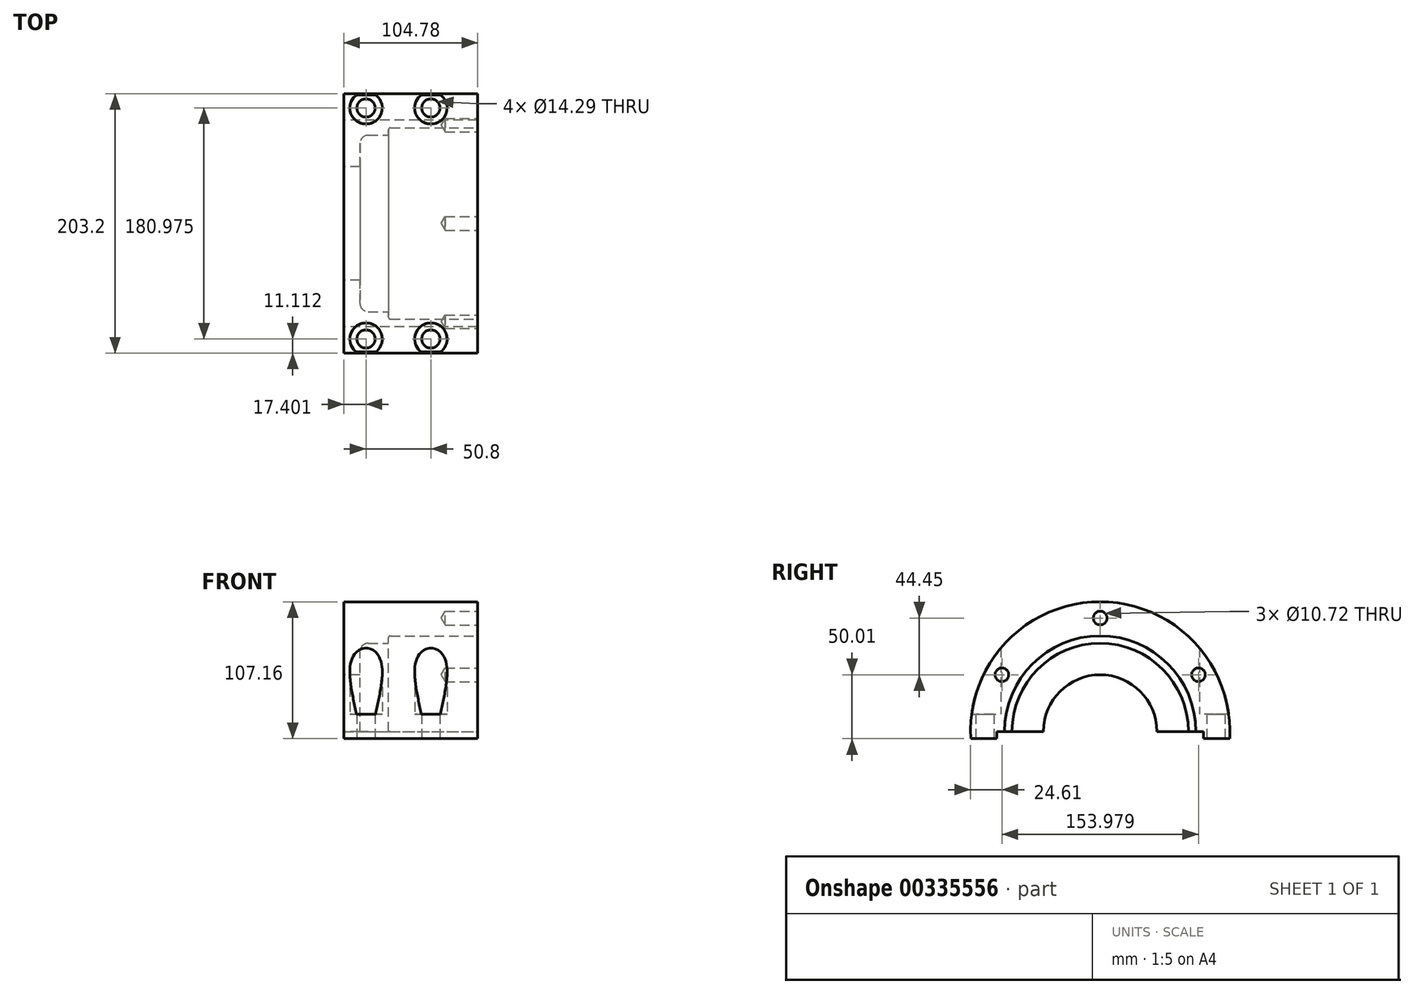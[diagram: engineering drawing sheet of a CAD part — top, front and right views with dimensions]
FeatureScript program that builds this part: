
annotation { "Feature Type Name" : "Feature", "Feature Type Description" : "" }
export const myFeature = defineFeature(function(context is Context, id is Id, definition is map)
    precondition{}
    {
        {
            var Q0;
            Q0=qCreatedBy(makeId("Right.planeOp"),FACE);
            var sketch = newSketch(context, id + "F0", { "sketchPlane" : qUnion([Q0])});
            skCircle(sketch, "E0", {"center": v(0, 0) * mm, "radius": 101.6 * mm});
            skCircle(sketch, "E1", {"center": v(0, 0) * mm, "radius": 44.45 * mm});
            skSolve(sketch);
        }
        {
            var Q0;
            Q0=qSketchRegion(id+"F0",true);
            extrude(context, id + "F1", {"entities" : qUnion([Q0]), "endBound" : BoundingType.SYMMETRIC, "depth" : 104.77 * mm});
        }
        {
            var Q0;
            Q0=makeQuery(id+"F1.opExtrude","CAP_FACE",FACE,{"disambiguationData":[OSD([sQuery(id+"F0.wireOp",EDGE,"E0"),sQuery(id+"F0.wireOp",EDGE,"E1")])],"isStart":false});
            var sketch = newSketch(context, id + "F2", { "sketchPlane" : qUnion([Q0])});
            skCircle(sketch, "E2", {"center": v(0, 0) * mm, "radius": 69.09 * mm});
            skSolve(sketch);
        }
        {
            var Q0;
            Q0=qSketchRegion(id+"F2",true);
            extrude(context, id + "F3", {"entities" : qUnion([Q0]), "operationType" : NewBodyOperationType.REMOVE, "oppositeDirection" : true, "depth" : 92.07 * mm});
        }
        {
            var Q0;
            Q0=makeQuery(id+"F1.opExtrude","CAP_FACE",FACE,{"disambiguationData":[OSD([sQuery(id+"F0.wireOp",EDGE,"E0"),sQuery(id+"F0.wireOp",EDGE,"E1")])],"isStart":false});
            var sketch = newSketch(context, id + "F4", { "sketchPlane" : qUnion([Q0])});
            skCircle(sketch, "E3", {"center": v(0, 0) * mm, "radius": 74.93 * mm});
            skSolve(sketch);
        }
        {
            var Q0;
            Q0=qSketchRegion(id+"F4",true);
            extrude(context, id + "F5", {"entities" : qUnion([Q0]), "operationType" : NewBodyOperationType.REMOVE, "oppositeDirection" : true, "depth" : 69.85 * mm});
        }
        {
            var Q0;
            Q0=makeQuery(id+"F3.boolean.opBoolean","COPY",EDGE,{"derivedFrom":makeQuery(id+"F3.opExtrude","CAP_EDGE",EDGE,{"disambiguationData":[OSD([sQuery(id+"F2.wireOp",EDGE,"E2")])],"isStart":false})});
            fillet(context, id + "F6", {"entities" : qUnion([Q0]), "radius" : 6.35 * mm, "tangentPropagation" : true, "allowEdgeOverflow" : false});
        }
        {
            var Q0;
            Q0=makeQuery(id+"F5.boolean.opBoolean","COPY",EDGE,{"derivedFrom":makeQuery(id+"F5.opExtrude","CAP_EDGE",EDGE,{"disambiguationData":[OSD([sQuery(id+"F4.wireOp",EDGE,"E3")])],"isStart":false})});
            fillet(context, id + "F7", {"entities" : qUnion([Q0]), "radius" : 1.59 * mm, "tangentPropagation" : true, "allowEdgeOverflow" : false});
        }
        {
            var Q0;
            Q0=makeQuery(id+"F1.opExtrude","CAP_FACE",FACE,{"disambiguationData":[OSD([sQuery(id+"F0.wireOp",EDGE,"E0"),sQuery(id+"F0.wireOp",EDGE,"E1")])],"isStart":false});
            var sketch = newSketch(context, id + "F8", { "sketchPlane" : qUnion([Q0])});
            skCircle(sketch, "E4", {"center": v(0, 0) * mm, "radius": 88.9 * mm, "construction": true});
            skLineSegment(sketch, "E5", {"start": v(0, 0) * mm, "end": v(0, 117.43) * mm, "construction": true});
            skLineSegment(sketch, "E6", {"start": v(0, 0) * mm, "end": v(-111.63, 64.45) * mm, "construction": true});
            skPoint(sketch, "E7", {"position": v(-76.99, 44.45) * mm});
            skPoint(sketch, "E8", {"position": v(0, 88.9) * mm});
            skPoint(sketch, "E9.MirrorP", {"position": v(76.99, 44.45) * mm});
            skSolve(sketch);
        }
        {
            var Q0;
            Q0=sQuery(id+"F8.wireOp",VERTEX,"E7");
            var Q1;
            Q1=sQuery(id+"F8.wireOp",VERTEX,"E8");
            var Q2;
            Q2=sQuery(id+"F8.wireOp",VERTEX,"E9.MirrorP");
            var Q3;
            Q3=makeQuery(id+"F1.opExtrude","SWEPT_BODY",BODY,{"disambiguationData":[OSD([sQuery(id+"F0.wireOp",EDGE,"E0"),sQuery(id+"F0.wireOp",EDGE,"E1")])]});
            hole(context, id + "F9", {"style" : HoleStyle.SIMPLE, "endStyle" : HoleEndStyle.BLIND, "standardTappedOrClearance" : lookupTablePath({ "standard" : "ANSI", "engagement" : "75%", "pitch" : "13 tpi", "size" : "1/2", "type" : "Tapped" }), "standardBlindInLast" : lookupTablePath({ "standard" : "ANSI", "engagement" : "75%", "pitch" : "13 tpi", "size" : "1/2", "type" : "Tapped" }), "holeDiameter" : 10.72 * mm, "showTappedDepth" : true, "holeDepth" : 25.4 * mm, "tappedDepth" : 19.53 * mm, "tapClearance" : 3, "locations" : qUnion([Q0, Q1, Q2]), "scope" : qUnion([Q3]), "majorDiameter" : 12.7 * mm});
        }
        {
            var Q0;
            Q0=makeQuery(id+"F1.opExtrude","CAP_FACE",FACE,{"disambiguationData":[OSD([sQuery(id+"F0.wireOp",EDGE,"E0"),sQuery(id+"F0.wireOp",EDGE,"E1")])],"isStart":false});
            var sketch = newSketch(context, id + "F10", { "sketchPlane" : qUnion([Q0])});
            skLineSegment(sketch, "E10", {"start": v(-153.72, 0) * mm, "end": v(137.98, 0) * mm, "construction": true});
            skLineSegment(sketch, "E11.0", {"start": v(-153.72, -5.56) * mm, "end": v(137.98, -5.56) * mm, "construction": true});
            skLineSegment(sketch, "E12.bottom", {"start": v(-150.99, -5.56) * mm, "end": v(143.45, -5.56) * mm});
            skLineSegment(sketch, "E12.top", {"start": v(-150.99, -114.35) * mm, "end": v(143.45, -114.35) * mm});
            skLineSegment(sketch, "E12.left", {"start": v(-150.99, -5.56) * mm, "end": v(-150.99, -114.35) * mm});
            skLineSegment(sketch, "E12.right", {"start": v(143.45, -5.56) * mm, "end": v(143.45, -114.35) * mm});
            skSolve(sketch);
        }
        {
            var Q0;
            Q0=qSketchRegion(id+"F10",true);
            extrude(context, id + "F11", {"entities" : qUnion([Q0]), "operationType" : NewBodyOperationType.REMOVE, "endBound" : BoundingType.THROUGH_ALL, "oppositeDirection" : true, "depth" : 25.4 * mm});
        }
        {
            var Q0;
            Q0=makeQuery(id+"F1.opExtrude","CAP_FACE",FACE,{"disambiguationData":[OSD([sQuery(id+"F0.wireOp",EDGE,"E0"),sQuery(id+"F0.wireOp",EDGE,"E1")])],"isStart":false});
            var sketch = newSketch(context, id + "F12", { "sketchPlane" : qUnion([Q0])});
            skLineSegment(sketch, "E13", {"start": v(-147.56, 0) * mm, "end": v(159.2, 0) * mm, "construction": true});
            skLineSegment(sketch, "E14", {"start": v(0, 129.5) * mm, "end": v(0, -54.35) * mm, "construction": true});
            skLineSegment(sketch, "E15.0", {"start": v(-80.96, 129.5) * mm, "end": v(-80.96, -54.35) * mm, "construction": true});
            skLineSegment(sketch, "E16.bottom", {"start": v(-80.96, 0) * mm, "end": v(80.96, 0) * mm});
            skLineSegment(sketch, "E16.top", {"start": v(-80.96, -25.4) * mm, "end": v(80.96, -25.4) * mm});
            skLineSegment(sketch, "E16.left", {"start": v(-80.96, 0) * mm, "end": v(-80.96, -25.4) * mm});
            skLineSegment(sketch, "E16.right", {"start": v(80.96, 0) * mm, "end": v(80.96, -25.4) * mm});
            skSolve(sketch);
        }
        {
            var Q0;
            Q0=qSketchRegion(id+"F12",true);
            extrude(context, id + "F13", {"entities" : qUnion([Q0]), "operationType" : NewBodyOperationType.REMOVE, "endBound" : BoundingType.THROUGH_ALL, "oppositeDirection" : true, "depth" : 25.4 * mm});
        }
        {
            var Q0;
            Q0=makeQuery(id+"F11.boolean.opBoolean","COPY",FACE,{"disambiguationData":[OD(0.0)],"derivedFrom":makeQuery(id+"F11.opExtrude","SWEPT_FACE",FACE,{"disambiguationData":[OSD([sQuery(id+"F10.wireOp",EDGE,"E12.bottom")])]})});
            var sketch = newSketch(context, id + "F14", { "sketchPlane" : qUnion([Q0])});
            skLineSegment(sketch, "E17.0", {"start": v(15.81, 101.45) * mm, "end": v(15.81, 80.96) * mm, "construction": true});
            skLineSegment(sketch, "E18.0", {"start": v(-34.99, 101.45) * mm, "end": v(-34.99, 80.96) * mm, "construction": true});
            skLineSegment(sketch, "E19", {"start": v(92.44, 0) * mm, "end": v(-99.97, 0) * mm, "construction": true});
            skLineSegment(sketch, "E20.0", {"start": v(92.44, 90.49) * mm, "end": v(-99.97, 90.49) * mm, "construction": true});
            skPoint(sketch, "E21", {"position": v(15.81, 90.49) * mm});
            skPoint(sketch, "E22", {"position": v(-34.99, 90.49) * mm});
            skPoint(sketch, "E23.MirrorP", {"position": v(15.81, -90.49) * mm});
            skPoint(sketch, "E24.MirrorP", {"position": v(-34.99, -90.49) * mm});
            skSolve(sketch);
        }
        {
            var Q0;
            Q0=sQuery(id+"F14.wireOp",VERTEX,"E21");
            var Q1;
            Q1=sQuery(id+"F14.wireOp",VERTEX,"E22");
            var Q2;
            Q2=sQuery(id+"F14.wireOp",VERTEX,"E23.MirrorP");
            var Q3;
            Q3=sQuery(id+"F14.wireOp",VERTEX,"E24.MirrorP");
            var Q4;
            Q4=makeQuery(id+"F1.opExtrude","SWEPT_BODY",BODY,{"disambiguationData":[OSD([sQuery(id+"F0.wireOp",EDGE,"E0"),sQuery(id+"F0.wireOp",EDGE,"E1")])]});
            hole(context, id + "F15", {"style" : HoleStyle.SIMPLE, "endStyle" : HoleEndStyle.THROUGH, "holeDiameter" : 14.29 * mm, "tappedDepth" : 19.54 * mm, "tapClearance" : 3, "locations" : qUnion([Q0, Q1, Q2, Q3]), "scope" : qUnion([Q4])});
        }
        {
            var Q0;
            Q0=makeQuery(id+"F11.boolean.opBoolean","COPY",FACE,{"disambiguationData":[OD(0.0)],"derivedFrom":makeQuery(id+"F11.opExtrude","SWEPT_FACE",FACE,{"disambiguationData":[OSD([sQuery(id+"F10.wireOp",EDGE,"E12.bottom")])]})});
            cPlane(context, id + "F16", {"entities" : qUnion([Q0]), "cplaneType" : CPlaneType.OFFSET, "offset" : 19.05 * mm, "oppositeDirection" : true, "width" : 152.4 * mm, "height" : 152.4 * mm});
        }
        {
            var Q0;
            Q0=qCreatedBy(id+"F16.planeOp",FACE);
            var sketch = newSketch(context, id + "F17", { "sketchPlane" : qUnion([Q0])});
            skLineSegment(sketch, "E25", {"start": v(-131.89, 0) * mm, "end": v(145.82, 0) * mm, "construction": true});
            skCircle(sketch, "E26.0", {"center": v(-34.99, 90.49) * mm, "radius": 7.14 * mm, "construction": true});
            skCircle(sketch, "E27.0", {"center": v(15.81, 90.49) * mm, "radius": 7.14 * mm, "construction": true});
            skCircle(sketch, "E28.0", {"center": v(15.81, -90.49) * mm, "radius": 7.14 * mm, "construction": true});
            skCircle(sketch, "E29.0", {"center": v(-34.99, -90.49) * mm, "radius": 7.14 * mm, "construction": true});
            skCircle(sketch, "E30", {"center": v(-34.99, 90.49) * mm, "radius": 12.7 * mm});
            skCircle(sketch, "E31", {"center": v(15.81, 90.49) * mm, "radius": 12.7 * mm});
            skCircle(sketch, "E32", {"center": v(-34.99, -90.49) * mm, "radius": 12.7 * mm});
            skCircle(sketch, "E33", {"center": v(15.81, -90.49) * mm, "radius": 12.7 * mm});
            skSolve(sketch);
        }
        {
            var Q0;
            Q0=qSketchRegion(id+"F17",true);
            extrude(context, id + "F18", {"entities" : qUnion([Q0]), "operationType" : NewBodyOperationType.REMOVE, "endBound" : BoundingType.THROUGH_ALL, "oppositeDirection" : true, "depth" : 25.4 * mm});
        }
    });
